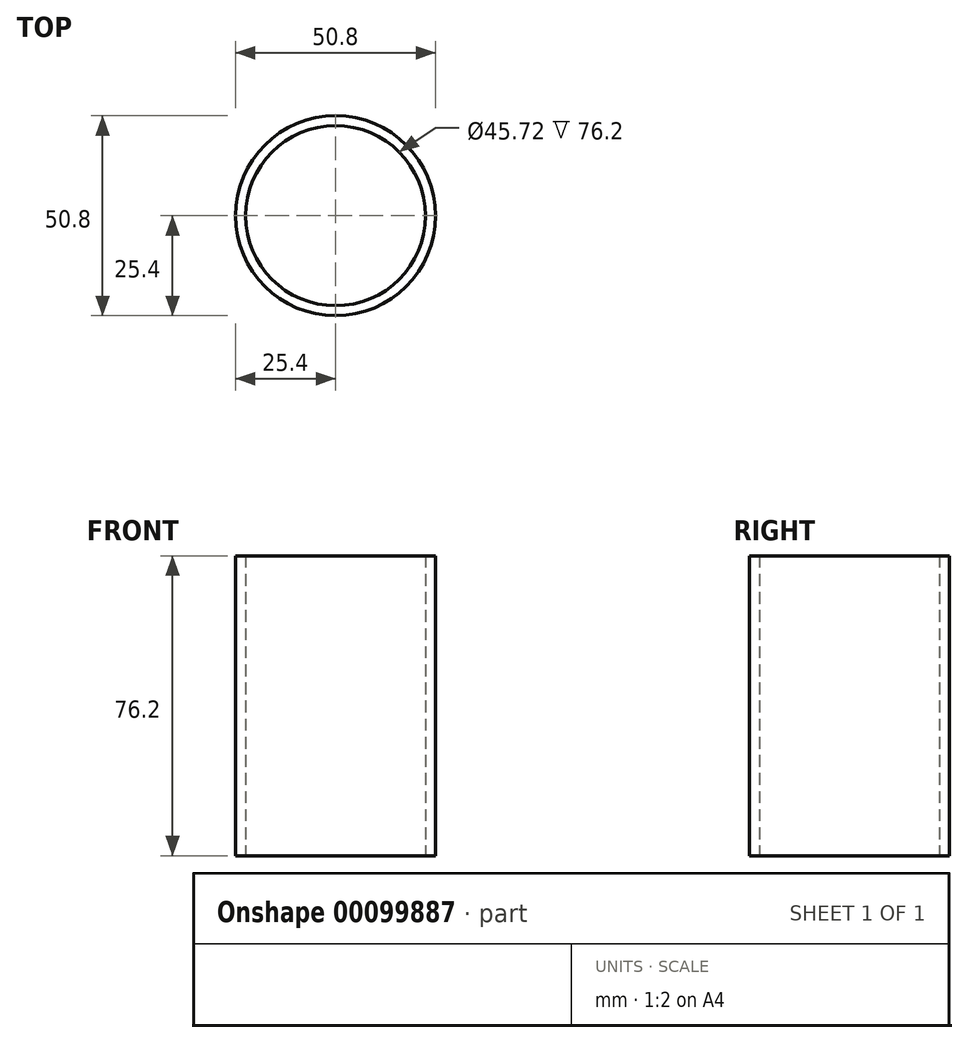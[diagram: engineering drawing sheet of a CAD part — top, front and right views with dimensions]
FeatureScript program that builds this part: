
annotation { "Feature Type Name" : "Feature", "Feature Type Description" : "" }
export const myFeature = defineFeature(function(context is Context, id is Id, definition is map)
    precondition{}
    {
        {
            var Q0;
            Q0=qCreatedBy(makeId("Top.planeOp"),FACE);
            var sketch = newSketch(context, id + "F0", { "sketchPlane" : qUnion([Q0])});
            skCircle(sketch, "E0", {"center": v(0, 0) * mm, "radius": 25.4 * mm});
            skSolve(sketch);
        }
        {
            var Q0;
            Q0 = qSketchRegion(id + "F0", true);
            extrude(context, id + "F1", {"entities" : qUnion([Q0]), "endBound" : BoundingType.SYMMETRIC, "depth" : 76.2 * mm});
        }
        {
            var Q0;
            Q0=makeQuery(id+"F1.opExtrude","CAP_FACE",FACE,{"disambiguationData":[OSD([sQuery(id+"F0.wireOp",EDGE,"E0")])],"isStart":false});
            var Q1;
            Q1=makeQuery(id+"F1.opExtrude","CAP_FACE",FACE,{"disambiguationData":[OSD([sQuery(id+"F0.wireOp",EDGE,"E0")])],"isStart":true});
            shell(context, id + "F2", {"entities" : qUnion([Q0, Q1]), "thickness" : 2.54 * mm});
        }
    });
